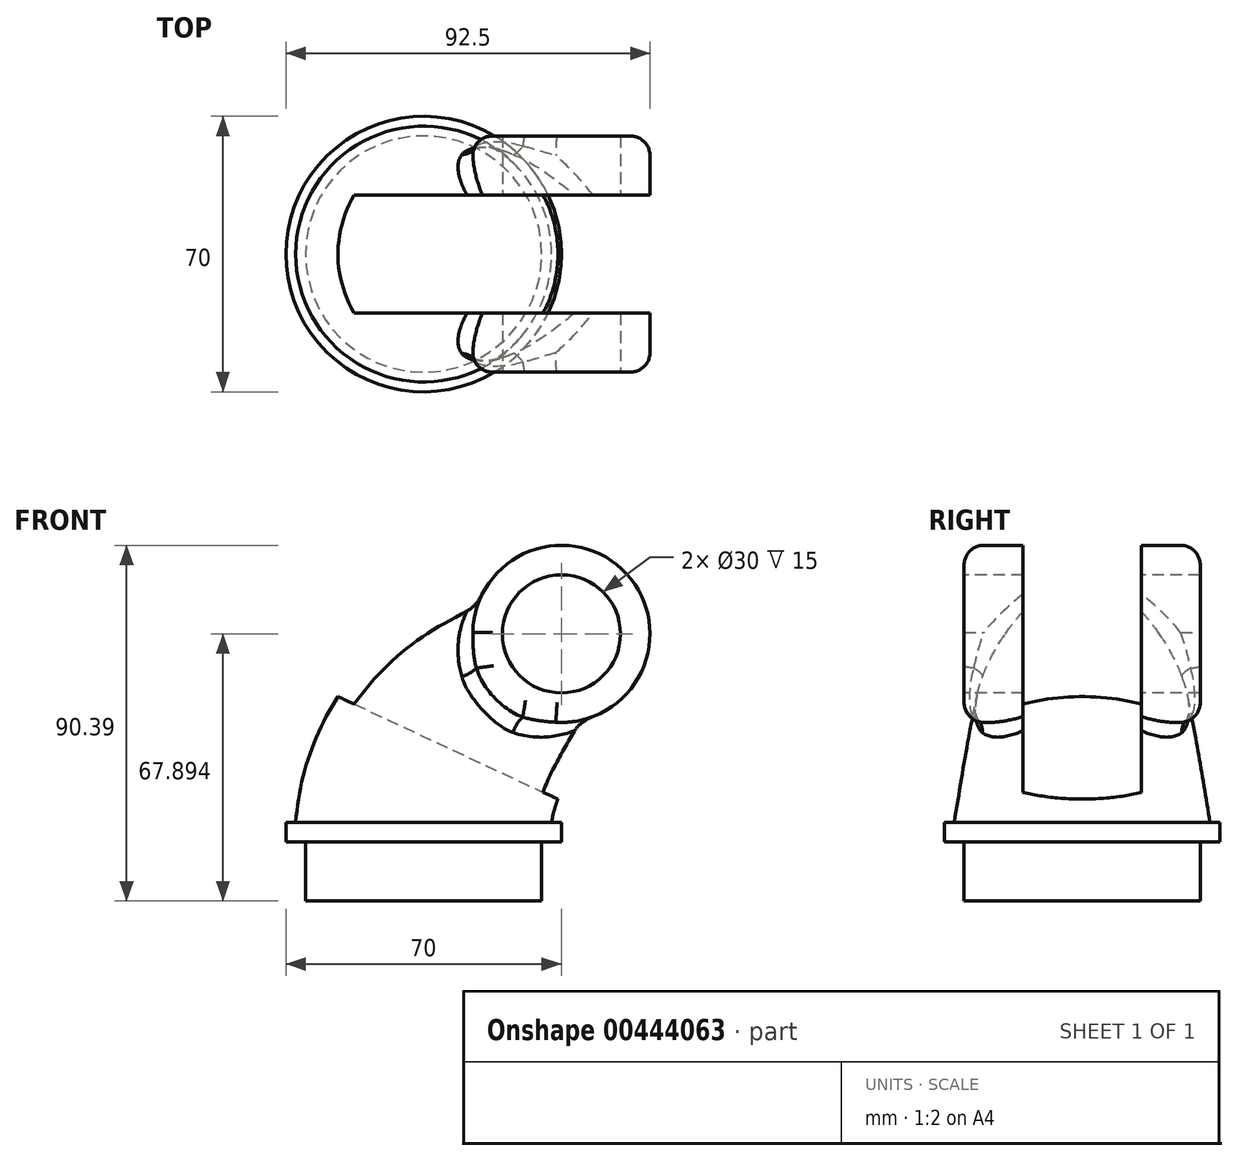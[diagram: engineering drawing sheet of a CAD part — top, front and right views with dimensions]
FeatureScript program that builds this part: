
annotation { "Feature Type Name" : "Feature", "Feature Type Description" : "" }
export const myFeature = defineFeature(function(context is Context, id is Id, definition is map)
    precondition{}
    {
        {
            var Q0;
            Q0=qCreatedBy(makeId("Top.planeOp"),FACE);
            var sketch = newSketch(context, id + "F0", { "sketchPlane" : qUnion([Q0])});
            skCircle(sketch, "E0", {"center": v(0, 0) * mm, "radius": 35 * mm});
            skSolve(sketch);
        }
        {
            var Q0;
            Q0 = qSketchRegion(id + "F0", true);
            extrude(context, id + "F1", {"entities" : qUnion([Q0]), "depth" : 5 * mm});
        }
        {
            var Q0;
            Q0=qCreatedBy(makeId("Front.planeOp"),FACE);
            var sketch = newSketch(context, id + "F2", { "sketchPlane" : qUnion([Q0])});
            skArc(sketch, "E1", {"start": v(17.6, 38.3) * mm, "mid": v(5.55, 23.37) * mm, "end": v(0, 5) * mm});
            skLineSegment(sketch, "E2", {"start": v(17.6, 38.3) * mm, "end": v(35, 52.9) * mm});
            skSolve(sketch);
        }
        {
            var Q0;
            Q0=sQuery(id+"F2.wireOp",EDGE,"E2");
            var Q1;
            Q1=sQuery(id+"F2.wireOp",VERTEX,"E2.end");
            cPlane(context, id + "F3", {"entities" : qUnion([Q0, Q1]), "cplaneType" : CPlaneType.LINE_POINT, "offset" : 25 * mm, "width" : 150 * mm, "height" : 150 * mm});
        }
        {
            var Q0;
            Q0=qCreatedBy(id+"F3.planeOp",FACE);
            var sketch = newSketch(context, id + "F4", { "sketchPlane" : qUnion([Q0])});
            skCircle(sketch, "E3", {"center": v(0, 18.02) * mm, "radius": 22.5 * mm});
            skSolve(sketch);
        }
        {
            var Q0;
            Q0=makeQuery(id+"F1.opExtrude","CAP_FACE",FACE,{"disambiguationData":[OSD([sQuery(id+"F0.wireOp",EDGE,"E0")])],"isStart":false});
            var sketch = newSketch(context, id + "F5", { "sketchPlane" : qUnion([Q0])});
            skCircle(sketch, "E4", {"center": v(0, 0) * mm, "radius": 32.5 * mm});
            skSolve(sketch);
        }
        {
            var Q0;
            Q0=qCreatedBy(makeId("Front.planeOp"),FACE);
            var sketch = newSketch(context, id + "F6", { "sketchPlane" : qUnion([Q0])});
            skArc(sketch, "E5", {"start": v(0.95, 58.66) * mm, "mid": v(-22.4, 35.96) * mm, "end": v(-32.5, 5) * mm});
            skLineSegment(sketch, "E6", {"start": v(0.95, 58.66) * mm, "end": v(20.54, 70.13) * mm});
            skSolve(sketch);
        }
        {
            var Q0;
            Q0=qCreatedBy(makeId("Front.planeOp"),FACE);
            var sketch = newSketch(context, id + "F7", { "sketchPlane" : qUnion([Q0])});
            skArc(sketch, "E7", {"start": v(37.05, 16.65) * mm, "mid": v(34.17, 11.06) * mm, "end": v(32.5, 5) * mm});
            skLineSegment(sketch, "E8", {"start": v(37.05, 16.65) * mm, "end": v(49.46, 35.66) * mm});
            skSolve(sketch);
        }
        {
            var Q1;
            Q1=makeQuery(id+"F5.imprint","IMPRINT",FACE,{"disambiguationData":[TD([[makeQuery(id+"F5.imprint","IMPRINT",EDGE,{"derivedFrom":sQuery(id+"F5.wireOp",EDGE,"E4")}),1.0]])]});
            var Q2;
            Q2=makeQuery(id+"F4.imprint","IMPRINT",FACE,{"disambiguationData":[TD([[makeQuery(id+"F4.imprint","IMPRINT",EDGE,{"derivedFrom":sQuery(id+"F4.wireOp",EDGE,"E3")}),1.0]])]});
            var Q3;
            Q3 = qConstructionFilter(qBodyType(qCreatedBy(id + "F7" ,EDGE), BodyType.WIRE), ConstructionObject.NO);
            var Q4;
            Q4 = qConstructionFilter(qBodyType(qCreatedBy(id + "F6" ,EDGE), BodyType.WIRE), ConstructionObject.NO);
            loft(context, id + "F8", {"operationType" : NewBodyOperationType.ADD, "addGuides" : true, "sheetProfilesArray" : [{ "sheetProfileEntities" : qUnion([Q1]) }, { "sheetProfileEntities" : qUnion([Q2]) }], "guidesArray" : [{ "guideEntities" : qUnion([Q3]), "guideDerivativeType" : LoftGuideDerivativeType.DEFAULT, "guideDerivativeMagnitude" : 1 }, { "guideEntities" : qUnion([Q4]), "guideDerivativeType" : LoftGuideDerivativeType.DEFAULT, "guideDerivativeMagnitude" : 1 }]});
        }
        {
            var Q0;
            Q0=qCreatedBy(makeId("Front.planeOp"),FACE);
            var sketch = newSketch(context, id + "F9", { "sketchPlane" : qUnion([Q0])});
            skCircle(sketch, "E9", {"center": v(35, 52.9) * mm, "radius": 22.5 * mm});
            skSolve(sketch);
        }
        {
            var Q0;
            Q0 = qSketchRegion(id + "F9", true);
            extrude(context, id + "F10", {"entities" : qUnion([Q0]), "operationType" : NewBodyOperationType.ADD, "endBound" : BoundingType.SYMMETRIC, "depth" : 60 * mm});
        }
        {
            var Q0;
            Q0=makeQuery(id+"F10.boolean.opBoolean","INTERSECT",EDGE,{"derivedFrom":[makeQuery(id+"F8.opLoft","SWEPT_FACE",FACE,{"disambiguationData":[OSD([sQuery(id+"F4.wireOp",EDGE,"E3"),sQuery(id+"F5.wireOp",EDGE,"E4"),sQuery(id+"F6.wireOp",VERTEX,"E6.start"),sQuery(id+"F6.wireOp",EDGE,"E5"),sQuery(id+"F6.wireOp",EDGE,"E6"),sQuery(id+"F7.wireOp",VERTEX,"E8.start"),sQuery(id+"F7.wireOp",EDGE,"E7"),sQuery(id+"F7.wireOp",EDGE,"E8")])]}),makeQuery(id+"F10.opExtrude","SWEPT_FACE",FACE,{"disambiguationData":[OSD([sQuery(id+"F9.wireOp",EDGE,"E9")])]})]});
            fillet(context, id + "F11", {"entities" : qUnion([Q0]), "radius" : 5 * mm, "tangentPropagation" : true, "allowEdgeOverflow" : false});
        }
        {
            var Q0;
            Q0=makeQuery(id+"F10.opExtrude","CAP_EDGE",EDGE,{"disambiguationData":[OSD([sQuery(id+"F9.wireOp",EDGE,"E9")])],"isStart":true});
            var Q1;
            Q1=makeQuery(id+"F10.opExtrude","CAP_EDGE",EDGE,{"disambiguationData":[OSD([sQuery(id+"F9.wireOp",EDGE,"E9")])],"isStart":false});
            fillet(context, id + "F12", {"entities" : qUnion([Q0, Q1]), "radius" : 5 * mm, "tangentPropagation" : true, "allowEdgeOverflow" : false});
        }
        {
            var Q0;
            Q0=makeQuery(id+"F10.opExtrude","CAP_FACE",FACE,{"disambiguationData":[OSD([sQuery(id+"F9.wireOp",EDGE,"E9")])],"isStart":false});
            var sketch = newSketch(context, id + "F13", { "sketchPlane" : qUnion([Q0])});
            skCircle(sketch, "E10", {"center": v(35, 52.9) * mm, "radius": 15 * mm});
            skSolve(sketch);
        }
        {
            var Q0;
            Q0 = qSketchRegion(id + "F13", true);
            extrude(context, id + "F14", {"entities" : qUnion([Q0]), "operationType" : NewBodyOperationType.REMOVE, "endBound" : BoundingType.THROUGH_ALL, "oppositeDirection" : true, "depth" : 25 * mm});
        }
        {
            var Q0;
            Q0=qCreatedBy(makeId("Front.planeOp"),FACE);
            var sketch = newSketch(context, id + "F15", { "sketchPlane" : qUnion([Q0])});
            skLineSegment(sketch, "E11", {"start": v(-104.18, 75.4) * mm, "end": v(57.5, 0) * mm});
            skLineSegment(sketch, "E12", {"start": v(57.5, 75.4) * mm, "end": v(57.5, 0) * mm});
            skLineSegment(sketch, "E13", {"start": v(-104.18, 75.4) * mm, "end": v(57.5, 75.4) * mm});
            skSolve(sketch);
        }
        {
            var Q0;
            Q0 = qSketchRegion(id + "F15", true);
            extrude(context, id + "F16", {"entities" : qUnion([Q0]), "operationType" : NewBodyOperationType.REMOVE, "endBound" : BoundingType.SYMMETRIC, "oppositeDirection" : true, "depth" : 30 * mm});
        }
        {
            var Q0;
            Q0=qCreatedBy(makeId("Front.planeOp"),FACE);
            var sketch = newSketch(context, id + "F17", { "sketchPlane" : qUnion([Q0])});
            skLineSegment(sketch, "E14.bottom", {"start": v(0, 0) * mm, "end": v(-30, 0) * mm});
            skLineSegment(sketch, "E14.top", {"start": v(0, -15) * mm, "end": v(-30, -15) * mm});
            skLineSegment(sketch, "E14.left", {"start": v(0, 0) * mm, "end": v(0, -15) * mm});
            skLineSegment(sketch, "E14.right", {"start": v(-30, 0) * mm, "end": v(-30, -15) * mm});
            skSolve(sketch);
        }
        {
            var Q0;
            Q0=makeQuery(id+"F17.imprint","IMPRINT",FACE,{"disambiguationData":[TD([[makeQuery(id+"F17.imprint","IMPRINT",EDGE,{"derivedFrom":sQuery(id+"F17.wireOp",EDGE,"E14.bottom")}),1.0]])]});
            var Q1;
            Q1=sQuery(id+"F17.wireOp",EDGE,"E14.left");
            revolve(context, id + "F18", {"operationType" : NewBodyOperationType.ADD, "entities" : qUnion([Q0]), "axis" : qUnion([Q1]), "revolveType" : RevolveType.FULL});
        }
    });
